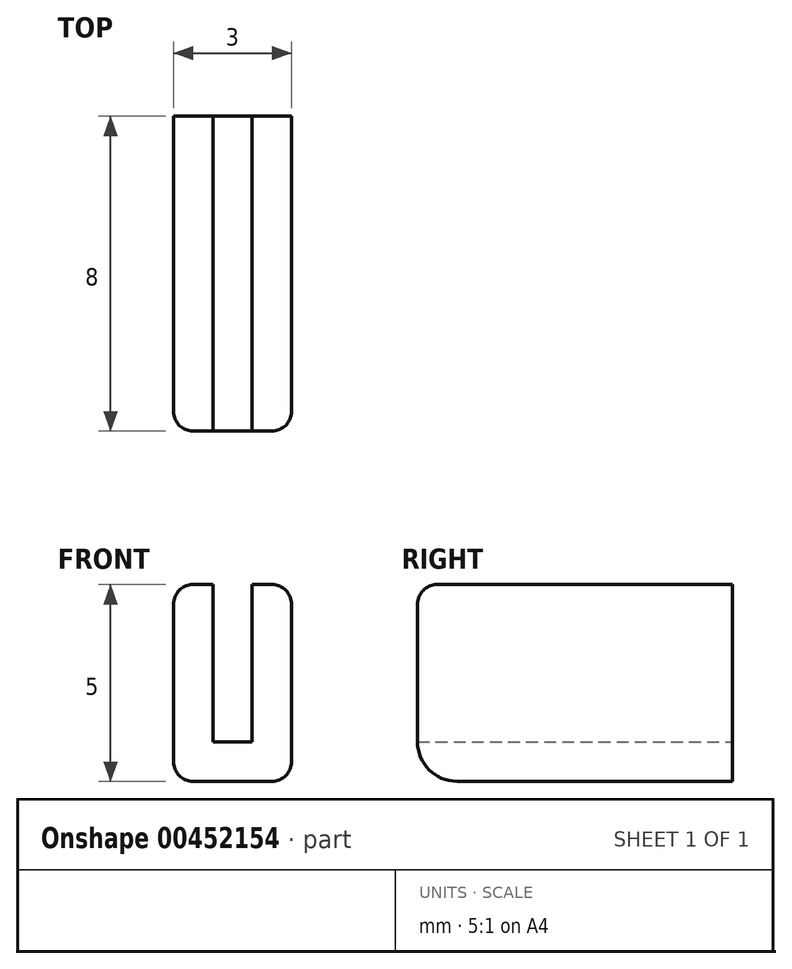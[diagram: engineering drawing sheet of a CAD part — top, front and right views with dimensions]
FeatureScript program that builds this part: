
annotation { "Feature Type Name" : "Feature", "Feature Type Description" : "" }
export const myFeature = defineFeature(function(context is Context, id is Id, definition is map)
    precondition{}
    {
        {
            var Q0;
            Q0=qCreatedBy(makeId("Front.planeOp"),FACE);
            var sketch = newSketch(context, id + "F0", { "sketchPlane" : qUnion([Q0])});
            skLineSegment(sketch, "E0.bottom", {"start": v(1.5, 2.5) * mm, "end": v(-1.5, 2.5) * mm});
            skLineSegment(sketch, "E0.top", {"start": v(1.5, -2.5) * mm, "end": v(-1.5, -2.5) * mm});
            skLineSegment(sketch, "E0.left", {"start": v(1.5, 2.5) * mm, "end": v(1.5, -2.5) * mm});
            skLineSegment(sketch, "E0.right", {"start": v(-1.5, 2.5) * mm, "end": v(-1.5, -2.5) * mm});
            skPoint(sketch, "E0.middle", {"position": v(0, 0) * mm});
            skLineSegment(sketch, "E1.bottom", {"start": v(0.5, -1.5) * mm, "end": v(-0.5, -1.5) * mm});
            skLineSegment(sketch, "E1.top", {"start": v(0.5, 6.5) * mm, "end": v(-0.5, 6.5) * mm});
            skLineSegment(sketch, "E1.left", {"start": v(0.5, -1.5) * mm, "end": v(0.5, 6.5) * mm});
            skLineSegment(sketch, "E1.right", {"start": v(-0.5, -1.5) * mm, "end": v(-0.5, 6.5) * mm});
            skPoint(sketch, "E1.middle", {"position": v(0, 2.5) * mm});
            skSolve(sketch);
        }
        {
            var Q0;
            Q0=makeQuery(id+"F0.imprint","IMPRINT",FACE,{"disambiguationData":[TD([[makeQuery(id+"F0.imprint","IMPRINT",EDGE,{"derivedFrom":sQuery(id+"F0.wireOp",EDGE,"E0.top")}),-1.0]])]});
            extrude(context, id + "F1", {"entities" : qUnion([Q0]), "depth" : 8 * mm, "offsetDistance" : 25 * mm});
        }
        {
            var Q0;
            Q0=makeQuery(id+"F1.opExtrude","CAP_EDGE",EDGE,{"disambiguationData":[OSD([sQuery(id+"F0.wireOp",EDGE,"E0.top")])],"isStart":false});
            fillet(context, id + "F2", {"entities" : qUnion([Q0]), "radius" : 1 * mm, "tangentPropagation" : true, "allowEdgeOverflow" : false});
        }
        {
            var Q0;
            Q0=makeQuery(id+"F1.opExtrude","SWEPT_EDGE",EDGE,{"disambiguationData":[OSD([sQuery(id+"F0.wireOp",EDGE,"E0.top"),sQuery(id+"F0.wireOp",EDGE,"E0.right")])]});
            var Q1;
            Q1=makeQuery(id+"F1.opExtrude","SWEPT_EDGE",EDGE,{"disambiguationData":[OSD([sQuery(id+"F0.wireOp",EDGE,"E0.top"),sQuery(id+"F0.wireOp",EDGE,"E0.left")])]});
            var Q2;
            Q2=makeQuery(id+"F1.opExtrude","SWEPT_EDGE",EDGE,{"disambiguationData":[OSD([sQuery(id+"F0.wireOp",EDGE,"E0.bottom"),sQuery(id+"F0.wireOp",EDGE,"E0.left")])]});
            var Q3;
            Q3=makeQuery(id+"F1.opExtrude","SWEPT_EDGE",EDGE,{"disambiguationData":[OSD([sQuery(id+"F0.wireOp",EDGE,"E0.bottom"),sQuery(id+"F0.wireOp",EDGE,"E0.right")])]});
            var Q4;
            {var subQ0=sQuery(id+"F0.wireOp",EDGE,"E0.bottom");Q4=makeQuery(id+"F1.opExtrude","CAP_EDGE",EDGE,{"disambiguationData":[OSD([subQ0]),TDD([makeQuery(id+"F0.imprint","IMPRINT",EDGE,{"disambiguationData":[TD([[makeQuery(id+"F0.imprint","INTERSECT",VERTEX,{"derivedFrom":[subQ0,sQuery(id+"F0.wireOp",EDGE,"E0.right")]}),1.0]])],"derivedFrom":subQ0})])],"isStart":false});}
            var Q5;
            {var subQ0=sQuery(id+"F0.wireOp",EDGE,"E0.bottom");Q5=makeQuery(id+"F1.opExtrude","CAP_EDGE",EDGE,{"disambiguationData":[OSD([subQ0]),TDD([makeQuery(id+"F0.imprint","IMPRINT",EDGE,{"disambiguationData":[TD([[makeQuery(id+"F0.imprint","INTERSECT",VERTEX,{"derivedFrom":[subQ0,sQuery(id+"F0.wireOp",EDGE,"E0.left")]}),-1.0]])],"derivedFrom":subQ0})])],"isStart":false});}
            fillet(context, id + "F3", {"entities" : qUnion([Q0, Q1, Q2, Q3, Q4, Q5]), "radius" : 0.5 * mm, "tangentPropagation" : true, "allowEdgeOverflow" : false});
        }
    });
